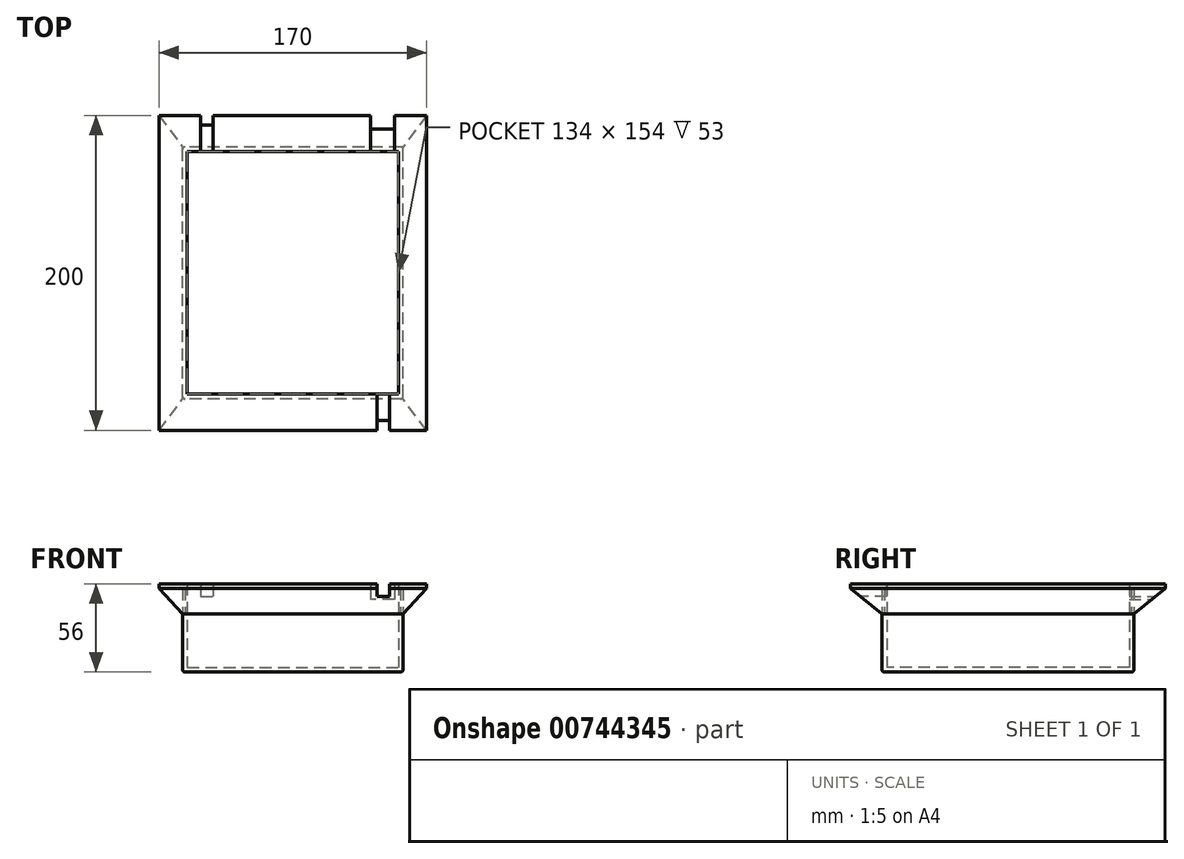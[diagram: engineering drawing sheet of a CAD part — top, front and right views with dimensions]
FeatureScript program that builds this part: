
annotation { "Feature Type Name" : "Feature", "Feature Type Description" : "" }
export const myFeature = defineFeature(function(context is Context, id is Id, definition is map)
    precondition{}
    {
        {
            var Q0;
            Q0=qCreatedBy(makeId("Top.planeOp"),FACE);
            var sketch = newSketch(context, id + "F0", { "sketchPlane" : qUnion([Q0])});
            skLineSegment(sketch, "E0.bottom", {"start": v(70, 80) * mm, "end": v(-70, 80) * mm});
            skLineSegment(sketch, "E0.top", {"start": v(70, -80) * mm, "end": v(-70, -80) * mm});
            skLineSegment(sketch, "E0.left", {"start": v(70, 80) * mm, "end": v(70, -80) * mm});
            skLineSegment(sketch, "E0.right", {"start": v(-70, 80) * mm, "end": v(-70, -80) * mm});
            skPoint(sketch, "E0.middle", {"position": v(0, 0) * mm});
            skSolve(sketch);
        }
        {
            var Q0;
            Q0=makeQuery(id+"F0.imprint","IMPRINT",FACE,{"disambiguationData":[TD([[makeQuery(id+"F0.imprint","IMPRINT",EDGE,{"derivedFrom":sQuery(id+"F0.wireOp",EDGE,"E0.bottom")}),1.0]])]});
            extrude(context, id + "F1", {"entities" : qUnion([Q0]), "depth" : 3 * mm, "offsetDistance" : 25 * mm});
        }
        {
            var Q0;
            Q0=makeQuery(id+"F1.opExtrude","CAP_FACE",FACE,{"disambiguationData":[OSD([sQuery(id+"F0.wireOp",EDGE,"E0.bottom"),sQuery(id+"F0.wireOp",EDGE,"E0.top"),sQuery(id+"F0.wireOp",EDGE,"E0.left"),sQuery(id+"F0.wireOp",EDGE,"E0.right")])],"isStart":false});
            var sketch = newSketch(context, id + "F2", { "sketchPlane" : qUnion([Q0])});
            skLineSegment(sketch, "E1.bottom", {"start": v(-70, 80) * mm, "end": v(70, 80) * mm});
            skLineSegment(sketch, "E1.top", {"start": v(-70, -80) * mm, "end": v(70, -80) * mm});
            skLineSegment(sketch, "E1.left", {"start": v(-70, 80) * mm, "end": v(-70, -80) * mm});
            skLineSegment(sketch, "E1.right", {"start": v(70, 80) * mm, "end": v(70, -80) * mm});
            skLineSegment(sketch, "E2.bottom", {"start": v(-67, 77) * mm, "end": v(67, 77) * mm});
            skLineSegment(sketch, "E2.top", {"start": v(-67, -77) * mm, "end": v(67, -77) * mm});
            skLineSegment(sketch, "E2.left", {"start": v(-67, 77) * mm, "end": v(-67, -77) * mm});
            skLineSegment(sketch, "E2.right", {"start": v(67, 77) * mm, "end": v(67, -77) * mm});
            skSolve(sketch);
        }
        {
            var Q0;
            Q0=makeQuery(id+"F2.imprint","IMPRINT",FACE,{"disambiguationData":[TD([[makeQuery(id+"F2.imprint","IMPRINT",EDGE,{"derivedFrom":sQuery(id+"F2.wireOp",EDGE,"E1.bottom")}),1.0]])]});
            extrude(context, id + "F3", {"entities" : qUnion([Q0]), "operationType" : NewBodyOperationType.ADD, "depth" : 50 * mm, "offsetDistance" : 25 * mm});
        }
        {
            var Q0;
            Q0=makeQuery(id+"F3.opExtrude","CAP_FACE",FACE,{"disambiguationData":[OSD([sQuery(id+"F2.wireOp",EDGE,"E1.bottom"),sQuery(id+"F2.wireOp",EDGE,"E1.top"),sQuery(id+"F2.wireOp",EDGE,"E1.left"),sQuery(id+"F2.wireOp",EDGE,"E1.right"),sQuery(id+"F2.wireOp",EDGE,"E2.bottom"),sQuery(id+"F2.wireOp",EDGE,"E2.top"),sQuery(id+"F2.wireOp",EDGE,"E2.left"),sQuery(id+"F2.wireOp",EDGE,"E2.right")])],"isStart":false});
            var sketch = newSketch(context, id + "F4", { "sketchPlane" : qUnion([Q0])});
            skLineSegment(sketch, "E3.bottom", {"start": v(-67, 77) * mm, "end": v(67, 77) * mm});
            skLineSegment(sketch, "E3.top", {"start": v(-67, -77) * mm, "end": v(67, -77) * mm});
            skLineSegment(sketch, "E3.left", {"start": v(-67, 77) * mm, "end": v(-67, -77) * mm});
            skLineSegment(sketch, "E3.right", {"start": v(67, 77) * mm, "end": v(67, -77) * mm});
            skLineSegment(sketch, "E4.bottom", {"start": v(-85, 100) * mm, "end": v(85, 100) * mm});
            skLineSegment(sketch, "E4.top", {"start": v(-85, -100) * mm, "end": v(85, -100) * mm});
            skLineSegment(sketch, "E4.left", {"start": v(-85, 100) * mm, "end": v(-85, -100) * mm});
            skLineSegment(sketch, "E4.right", {"start": v(85, 100) * mm, "end": v(85, -100) * mm});
            skPoint(sketch, "E5", {"position": v(0, 100) * mm});
            skPoint(sketch, "E6", {"position": v(85, 0) * mm});
            skSolve(sketch);
        }
        {
            var Q0;
            Q0=makeQuery(id+"F4.imprint","IMPRINT",FACE,{"disambiguationData":[TD([[makeQuery(id+"F4.imprint","IMPRINT",EDGE,{"derivedFrom":sQuery(id+"F4.wireOp",EDGE,"E4.bottom")}),-1.0]])]});
            var Q1;
            Q1=makeQuery(id+"F4.imprint","IMPRINT",FACE,{"disambiguationData":[TD([[makeQuery(id+"F4.imprint","IMPRINT",EDGE,{"derivedFrom":sQuery(id+"F4.wireOp",EDGE,"E3.bottom")}),1.0]])]});
            extrude(context, id + "F5", {"entities" : qUnion([Q0, Q1]), "operationType" : NewBodyOperationType.ADD, "depth" : 3 * mm, "offsetDistance" : 25 * mm});
        }
        {
            var Q0;
            Q0=makeQuery(id+"F5.opExtrude","SWEPT_FACE",FACE,{"disambiguationData":[OSD([sQuery(id+"F4.wireOp",EDGE,"E4.bottom")])]});
            var sketch = newSketch(context, id + "F6", { "sketchPlane" : qUnion([Q0])});
            skLineSegment(sketch, "E7.bottom", {"start": v(-64.5, 56) * mm, "end": v(-49.5, 56) * mm});
            skLineSegment(sketch, "E7.top", {"start": v(-64.5, 46) * mm, "end": v(-49.5, 46) * mm});
            skLineSegment(sketch, "E7.left", {"start": v(-64.5, 56) * mm, "end": v(-64.5, 46) * mm});
            skLineSegment(sketch, "E7.right", {"start": v(-49.5, 56) * mm, "end": v(-49.5, 46) * mm});
            skLineSegment(sketch, "E8.bottom", {"start": v(58.58, 56) * mm, "end": v(50.58, 56) * mm});
            skLineSegment(sketch, "E8.top", {"start": v(58.58, 48) * mm, "end": v(50.58, 48) * mm});
            skLineSegment(sketch, "E8.left", {"start": v(58.58, 56) * mm, "end": v(58.58, 48) * mm});
            skLineSegment(sketch, "E8.right", {"start": v(50.58, 56) * mm, "end": v(50.58, 48) * mm});
            skSolve(sketch);
        }
        {
            var Q0;
            Q0=makeQuery(id+"F5.opExtrude","SWEPT_FACE",FACE,{"disambiguationData":[OSD([sQuery(id+"F4.wireOp",EDGE,"E4.top")])]});
            var sketch = newSketch(context, id + "F7", { "sketchPlane" : qUnion([Q0])});
            skLineSegment(sketch, "E9.bottom", {"start": v(61.57, 56) * mm, "end": v(53.57, 56) * mm});
            skLineSegment(sketch, "E9.top", {"start": v(61.57, 48) * mm, "end": v(53.57, 48) * mm});
            skLineSegment(sketch, "E9.left", {"start": v(61.57, 56) * mm, "end": v(61.57, 48) * mm});
            skLineSegment(sketch, "E9.right", {"start": v(53.57, 56) * mm, "end": v(53.57, 48) * mm});
            skSolve(sketch);
        }
        {
            var Q0;
            Q0=makeQuery(id+"F1.opExtrude","CAP_EDGE",EDGE,{"disambiguationData":[OSD([sQuery(id+"F0.wireOp",EDGE,"E0.right")])],"isStart":true});
            var Q1;
            Q1=makeQuery(id+"F1.opExtrude","CAP_EDGE",EDGE,{"disambiguationData":[OSD([sQuery(id+"F0.wireOp",EDGE,"E0.top")])],"isStart":true});
            var Q2;
            Q2=makeQuery(id+"F1.opExtrude","CAP_EDGE",EDGE,{"disambiguationData":[OSD([sQuery(id+"F0.wireOp",EDGE,"E0.left")])],"isStart":true});
            var Q3;
            Q3=makeQuery(id+"F1.opExtrude","CAP_EDGE",EDGE,{"disambiguationData":[OSD([sQuery(id+"F0.wireOp",EDGE,"E0.bottom")])],"isStart":true});
            var Q4;
            Q4=makeQuery(id+"F3.boolean.opBoolean","MERGE",EDGE,{"derivedFrom":[makeQuery(id+"F1.opExtrude","SWEPT_EDGE",EDGE,{"disambiguationData":[OSD([sQuery(id+"F0.wireOp",EDGE,"E0.bottom"),sQuery(id+"F0.wireOp",EDGE,"E0.right")])]}),makeQuery(id+"F3.opExtrude","SWEPT_EDGE",EDGE,{"disambiguationData":[OSD([sQuery(id+"F2.wireOp",EDGE,"E1.bottom"),sQuery(id+"F2.wireOp",EDGE,"E1.left")])]})]});
            var Q5;
            Q5=makeQuery(id+"F3.boolean.opBoolean","MERGE",EDGE,{"derivedFrom":[makeQuery(id+"F1.opExtrude","SWEPT_EDGE",EDGE,{"disambiguationData":[OSD([sQuery(id+"F0.wireOp",EDGE,"E0.bottom"),sQuery(id+"F0.wireOp",EDGE,"E0.left")])]}),makeQuery(id+"F3.opExtrude","SWEPT_EDGE",EDGE,{"disambiguationData":[OSD([sQuery(id+"F2.wireOp",EDGE,"E1.bottom"),sQuery(id+"F2.wireOp",EDGE,"E1.right")])]})]});
            var Q6;
            Q6=makeQuery(id+"F3.boolean.opBoolean","MERGE",EDGE,{"derivedFrom":[makeQuery(id+"F1.opExtrude","SWEPT_EDGE",EDGE,{"disambiguationData":[OSD([sQuery(id+"F0.wireOp",EDGE,"E0.top"),sQuery(id+"F0.wireOp",EDGE,"E0.right")])]}),makeQuery(id+"F3.opExtrude","SWEPT_EDGE",EDGE,{"disambiguationData":[OSD([sQuery(id+"F2.wireOp",EDGE,"E1.top"),sQuery(id+"F2.wireOp",EDGE,"E1.left")])]})]});
            var Q7;
            Q7=makeQuery(id+"F3.boolean.opBoolean","MERGE",EDGE,{"derivedFrom":[makeQuery(id+"F1.opExtrude","SWEPT_EDGE",EDGE,{"disambiguationData":[OSD([sQuery(id+"F0.wireOp",EDGE,"E0.top"),sQuery(id+"F0.wireOp",EDGE,"E0.left")])]}),makeQuery(id+"F3.opExtrude","SWEPT_EDGE",EDGE,{"disambiguationData":[OSD([sQuery(id+"F2.wireOp",EDGE,"E1.top"),sQuery(id+"F2.wireOp",EDGE,"E1.right")])]})]});
            fillet(context, id + "F8", {"entities" : qUnion([Q0, Q1, Q2, Q3, Q4, Q5, Q6, Q7]), "radius" : 1.5 * mm, "tangentPropagation" : true, "allowEdgeOverflow" : false});
        }
        {
            var Q0;
            Q0=makeQuery(id+"F5.opExtrude","SWEPT_FACE",FACE,{"disambiguationData":[OSD([sQuery(id+"F4.wireOp",EDGE,"E4.left")])]});
            var sketch = newSketch(context, id + "F9", { "sketchPlane" : qUnion([Q0])});
            skLineSegment(sketch, "E10", {"start": v(-100, 53) * mm, "end": v(-80, 36.93) * mm});
            skLineSegment(sketch, "E11", {"start": v(-80, 36.93) * mm, "end": v(-80, 53) * mm});
            skLineSegment(sketch, "E12", {"start": v(-80, 53) * mm, "end": v(-100, 53) * mm});
            skLineSegment(sketch, "E13.MirrorCS", {"start": v(100, 53) * mm, "end": v(80, 36.93) * mm});
            skLineSegment(sketch, "E14.MirrorCS", {"start": v(80, 36.93) * mm, "end": v(80, 53) * mm});
            skLineSegment(sketch, "E15.MirrorCS", {"start": v(80, 53) * mm, "end": v(100, 53) * mm});
            skSolve(sketch);
        }
        {
            var Q0;
            Q0=makeQuery(id+"F9.imprint","IMPRINT",FACE,{"disambiguationData":[TD([[makeQuery(id+"F9.imprint","IMPRINT",EDGE,{"derivedFrom":sQuery(id+"F9.wireOp",EDGE,"E10")}),1.0]])]});
            var Q1;
            Q1=makeQuery(id+"F9.imprint","IMPRINT",FACE,{"disambiguationData":[TD([[makeQuery(id+"F9.imprint","IMPRINT",EDGE,{"derivedFrom":sQuery(id+"F9.wireOp",EDGE,"E13.MirrorCS")}),-1.0]])]});
            var Q2;
            Q2=makeQuery(id+"F5.opExtrude","SWEPT_FACE",FACE,{"disambiguationData":[OSD([sQuery(id+"F4.wireOp",EDGE,"E4.right")])]});
            extrude(context, id + "F10", {"entities" : qUnion([Q0, Q1]), "operationType" : NewBodyOperationType.ADD, "endBound" : BoundingType.UP_TO_SURFACE, "oppositeDirection" : true, "depth" : 25 * mm, "endBoundEntityFace" : qUnion([Q2]), "offsetDistance" : 25 * mm});
        }
        {
            var Q0;
            {var subQ0=sQuery(id+"F6.wireOp",EDGE,"E7.top");Q0=makeQuery(id+"F6.imprint","IMPRINT",FACE,{"disambiguationData":[TD([[makeQuery(id+"F6.imprint","IMPRINT",EDGE,{"derivedFrom":subQ0}),1.0]])]});}
            var Q1;
            {var subQ0=sQuery(id+"F6.wireOp",EDGE,"E7.bottom");Q1=makeQuery(id+"F6.imprint","IMPRINT",FACE,{"disambiguationData":[TD([[makeQuery(id+"F6.imprint","IMPRINT",EDGE,{"derivedFrom":subQ0}),1.0]])]});}
            var Q2;
            {var subQ0=sQuery(id+"F6.wireOp",EDGE,"E8.top");Q2=makeQuery(id+"F6.imprint","IMPRINT",FACE,{"disambiguationData":[TD([[makeQuery(id+"F6.imprint","IMPRINT",EDGE,{"derivedFrom":subQ0}),-1.0]])]});}
            var Q3;
            {var subQ0=sQuery(id+"F6.wireOp",EDGE,"E8.bottom");Q3=makeQuery(id+"F6.imprint","IMPRINT",FACE,{"disambiguationData":[TD([[makeQuery(id+"F6.imprint","IMPRINT",EDGE,{"derivedFrom":subQ0}),1.0]])]});}
            extrude(context, id + "F11", {"entities" : qUnion([Q0, Q1, Q2, Q3]), "operationType" : NewBodyOperationType.REMOVE, "oppositeDirection" : true, "depth" : 25 * mm, "offsetDistance" : 25 * mm});
        }
        {
            var Q0;
            {var subQ0=sQuery(id+"F7.wireOp",EDGE,"E9.top");Q0=makeQuery(id+"F7.imprint","IMPRINT",FACE,{"disambiguationData":[TD([[makeQuery(id+"F7.imprint","IMPRINT",EDGE,{"derivedFrom":subQ0}),-1.0]])]});}
            var Q1;
            {var subQ0=sQuery(id+"F7.wireOp",EDGE,"E9.bottom");Q1=makeQuery(id+"F7.imprint","IMPRINT",FACE,{"disambiguationData":[TD([[makeQuery(id+"F7.imprint","IMPRINT",EDGE,{"derivedFrom":subQ0}),-1.0]])]});}
            extrude(context, id + "F12", {"entities" : qUnion([Q0, Q1]), "operationType" : NewBodyOperationType.REMOVE, "oppositeDirection" : true, "depth" : 25 * mm, "offsetDistance" : 25 * mm});
        }
        {
            var Q0;
            {var subQ0=sQuery(id+"F4.wireOp",EDGE,"E4.right");var subQ1=sQuery(id+"F4.wireOp",EDGE,"E4.bottom");Q0=makeQuery(id+"F11.boolean.opBoolean","SPLIT",FACE,{"disambiguationData":[TD([makeQuery(id+"F5.opExtrude","SWEPT_FACE",FACE,{"disambiguationData":[OSD([subQ0])]})])],"derivedFrom":makeQuery(id+"F5.opExtrude","SWEPT_FACE",FACE,{"disambiguationData":[OSD([subQ1])]})});}
            var sketch = newSketch(context, id + "F13", { "sketchPlane" : qUnion([Q0])});
            skLineSegment(sketch, "E16", {"start": v(-85, 53) * mm, "end": v(-70, 36.93) * mm});
            skLineSegment(sketch, "E17", {"start": v(-70, 36.93) * mm, "end": v(-70, 53) * mm});
            skLineSegment(sketch, "E18", {"start": v(-70, 53) * mm, "end": v(-85, 53) * mm});
            skLineSegment(sketch, "E19.MirrorCS", {"start": v(70, 36.93) * mm, "end": v(70, 53) * mm});
            skLineSegment(sketch, "E20.MirrorCS", {"start": v(85, 53) * mm, "end": v(70, 36.93) * mm});
            skLineSegment(sketch, "E21.MirrorCS", {"start": v(70, 53) * mm, "end": v(85, 53) * mm});
            skSolve(sketch);
        }
        {
            var Q0;
            Q0=makeQuery(id+"F13.imprint","IMPRINT",FACE,{"disambiguationData":[TD([[makeQuery(id+"F13.imprint","IMPRINT",EDGE,{"derivedFrom":sQuery(id+"F13.wireOp",EDGE,"E16")}),1.0]])]});
            var Q1;
            Q1=makeQuery(id+"F13.imprint","IMPRINT",FACE,{"disambiguationData":[TD([[makeQuery(id+"F13.imprint","IMPRINT",EDGE,{"derivedFrom":sQuery(id+"F13.wireOp",EDGE,"E19.MirrorCS")}),-1.0]])]});
            var Q2;
            {var subQ0=sQuery(id+"F4.wireOp",EDGE,"E4.right");var subQ1=sQuery(id+"F4.wireOp",EDGE,"E4.top");Q2=makeQuery(id+"F12.boolean.opBoolean","SPLIT",FACE,{"disambiguationData":[TD([makeQuery(id+"F5.opExtrude","SWEPT_FACE",FACE,{"disambiguationData":[OSD([subQ0])]})])],"derivedFrom":makeQuery(id+"F5.opExtrude","SWEPT_FACE",FACE,{"disambiguationData":[OSD([subQ1])]})});}
            extrude(context, id + "F14", {"entities" : qUnion([Q0, Q1]), "operationType" : NewBodyOperationType.ADD, "endBound" : BoundingType.UP_TO_SURFACE, "oppositeDirection" : true, "depth" : 25 * mm, "endBoundEntityFace" : qUnion([Q2]), "offsetDistance" : 25 * mm});
        }
        {
            var Q0;
            {var subQ0=sQuery(id+"F4.wireOp",EDGE,"E4.right");var subQ1=sQuery(id+"F4.wireOp",EDGE,"E4.bottom");Q0=makeQuery(id+"F14.boolean.opBoolean","MERGE",FACE,{"derivedFrom":[makeQuery(id+"F11.boolean.opBoolean","SPLIT",FACE,{"disambiguationData":[TD([makeQuery(id+"F5.opExtrude","SWEPT_FACE",FACE,{"disambiguationData":[OSD([subQ0])]})])],"derivedFrom":makeQuery(id+"F5.opExtrude","SWEPT_FACE",FACE,{"disambiguationData":[OSD([subQ1])]})}),makeQuery(id+"F14.opExtrude","CAP_FACE",FACE,{"disambiguationData":[OSD([sQuery(id+"F13.wireOp",EDGE,"E16"),sQuery(id+"F13.wireOp",EDGE,"E17"),sQuery(id+"F13.wireOp",EDGE,"E18")])],"isStart":true})]});}
            var sketch = newSketch(context, id + "F15", { "sketchPlane" : qUnion([Q0])});
            skLineSegment(sketch, "E22", {"start": v(-85, 53) * mm, "end": v(-70, 36.93) * mm});
            skLineSegment(sketch, "E23", {"start": v(-70, 36.93) * mm, "end": v(-85, 36.93) * mm});
            skLineSegment(sketch, "E24", {"start": v(-85, 36.93) * mm, "end": v(-85, 53) * mm});
            skLineSegment(sketch, "E25.MirrorCS", {"start": v(85, 53) * mm, "end": v(70, 36.93) * mm});
            skLineSegment(sketch, "E26.MirrorCS", {"start": v(85, 36.93) * mm, "end": v(85, 53) * mm});
            skLineSegment(sketch, "E27.MirrorCS", {"start": v(70, 36.93) * mm, "end": v(85, 36.93) * mm});
            skSolve(sketch);
        }
        {
            var Q0;
            Q0=makeQuery(id+"F15.imprint","IMPRINT",FACE,{"disambiguationData":[TD([[makeQuery(id+"F15.imprint","IMPRINT",EDGE,{"derivedFrom":sQuery(id+"F15.wireOp",EDGE,"E22")}),-1.0]])]});
            var Q1;
            Q1=makeQuery(id+"F15.imprint","IMPRINT",FACE,{"disambiguationData":[TD([[makeQuery(id+"F15.imprint","IMPRINT",EDGE,{"derivedFrom":sQuery(id+"F15.wireOp",EDGE,"E25.MirrorCS")}),1.0]])]});
            var Q2;
            {var subQ1=sQuery(id+"F4.wireOp",EDGE,"E4.left");var subQ2=sQuery(id+"F4.wireOp",EDGE,"E4.top");Q2=makeQuery(id+"F14.boolean.opBoolean","MERGE",FACE,{"derivedFrom":[makeQuery(id+"F12.boolean.opBoolean","SPLIT",FACE,{"disambiguationData":[TD([makeQuery(id+"F5.opExtrude","SWEPT_FACE",FACE,{"disambiguationData":[OSD([subQ1])]})])],"derivedFrom":makeQuery(id+"F5.opExtrude","SWEPT_FACE",FACE,{"disambiguationData":[OSD([subQ2])]})}),makeQuery(id+"F14.opExtrude","CAP_FACE",FACE,{"disambiguationData":[OSD([sQuery(id+"F13.wireOp",EDGE,"E19.MirrorCS"),sQuery(id+"F13.wireOp",EDGE,"E20.MirrorCS"),sQuery(id+"F13.wireOp",EDGE,"E21.MirrorCS")])],"isStart":false})]});}
            extrude(context, id + "F16", {"entities" : qUnion([Q0, Q1]), "operationType" : NewBodyOperationType.REMOVE, "endBound" : BoundingType.UP_TO_SURFACE, "oppositeDirection" : true, "depth" : 25 * mm, "endBoundEntityFace" : qUnion([Q2]), "offsetDistance" : 25 * mm});
        }
        {
            var Q0;
            {var subQ0=sQuery(id+"F4.wireOp",EDGE,"E4.right");Q0=makeQuery(id+"F10.boolean.opBoolean","MERGE",FACE,{"derivedFrom":[makeQuery(id+"F5.opExtrude","SWEPT_FACE",FACE,{"disambiguationData":[OSD([subQ0])]}),makeQuery(id+"F10.opExtrude","CAP_FACE",FACE,{"disambiguationData":[OSD([subQ0]),OD(0.0)],"isStart":false}),makeQuery(id+"F10.opExtrude","CAP_FACE",FACE,{"disambiguationData":[OSD([subQ0]),OD(1.0)],"isStart":false})]});}
            var sketch = newSketch(context, id + "F17", { "sketchPlane" : qUnion([Q0])});
            skLineSegment(sketch, "E28", {"start": v(-100, 53) * mm, "end": v(-80, 36.93) * mm});
            skLineSegment(sketch, "E29", {"start": v(-80, 36.93) * mm, "end": v(-100, 36.93) * mm});
            skLineSegment(sketch, "E30", {"start": v(-100, 36.93) * mm, "end": v(-100, 53) * mm});
            skLineSegment(sketch, "E31.MirrorCS", {"start": v(100, 53) * mm, "end": v(80, 36.93) * mm});
            skLineSegment(sketch, "E32.MirrorCS", {"start": v(100, 36.93) * mm, "end": v(100, 53) * mm});
            skLineSegment(sketch, "E33.MirrorCS", {"start": v(80, 36.93) * mm, "end": v(100, 36.93) * mm});
            skSolve(sketch);
        }
        {
            var Q0;
            Q0=makeQuery(id+"F17.imprint","IMPRINT",FACE,{"disambiguationData":[TD([[makeQuery(id+"F17.imprint","IMPRINT",EDGE,{"derivedFrom":sQuery(id+"F17.wireOp",EDGE,"E28")}),-1.0]])]});
            var Q1;
            Q1=makeQuery(id+"F17.imprint","IMPRINT",FACE,{"disambiguationData":[TD([[makeQuery(id+"F17.imprint","IMPRINT",EDGE,{"derivedFrom":sQuery(id+"F17.wireOp",EDGE,"E31.MirrorCS")}),1.0]])]});
            var Q2;
            Q2=makeQuery(id+"F10.boolean.opBoolean","MERGE",FACE,{"derivedFrom":[makeQuery(id+"F5.opExtrude","SWEPT_FACE",FACE,{"disambiguationData":[OSD([sQuery(id+"F4.wireOp",EDGE,"E4.left")])]}),makeQuery(id+"F10.opExtrude","CAP_FACE",FACE,{"disambiguationData":[OSD([sQuery(id+"F9.wireOp",EDGE,"E10"),sQuery(id+"F9.wireOp",EDGE,"E11"),sQuery(id+"F9.wireOp",EDGE,"E12")])],"isStart":true}),makeQuery(id+"F10.opExtrude","CAP_FACE",FACE,{"disambiguationData":[OSD([sQuery(id+"F9.wireOp",EDGE,"E13.MirrorCS"),sQuery(id+"F9.wireOp",EDGE,"E14.MirrorCS"),sQuery(id+"F9.wireOp",EDGE,"E15.MirrorCS")])],"isStart":true})]});
            extrude(context, id + "F18", {"entities" : qUnion([Q0, Q1]), "operationType" : NewBodyOperationType.REMOVE, "endBound" : BoundingType.UP_TO_SURFACE, "oppositeDirection" : true, "depth" : 25 * mm, "endBoundEntityFace" : qUnion([Q2]), "offsetDistance" : 25 * mm});
        }
    });
